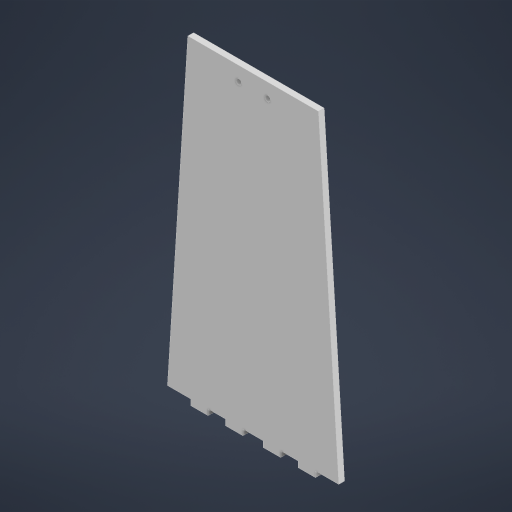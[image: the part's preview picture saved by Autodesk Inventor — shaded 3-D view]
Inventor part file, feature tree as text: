
AUTODESK INVENTOR PART (.ipt)
format: ipt  version: 2023.2 (Build 272271000, 271)  size: 237,056 bytes
history: native  units: mm
features: sketch x2
ambient origin geometry x8: Origin, YZ Plane, XZ Plane, XY Plane, X Axis, Y Axis, Z Axis, Center Point
bodies: Body1 (feature_tree)
feature tree (2):
  sketch  "Sketch1"  dims[d229=90.0mm]
  sketch  "Sketch2"  dims[d232=16.0mm d233=12.0mm d234=12.0mm d235=4.0mm d237=4.0mm d238=0.0mm d239=14.0mm d241=220.0mm d242=4.0mm d244=10.0mm d245=20.0mm d246=4.0mm d247=0.0mm d9=0.5mm d10=0.872665mm d11=0.5mm d12=0.872665mm d13=0.5mm d14=0.872665mm d27=0.5mm d28=0.872665mm d29=0.5mm d30=0.872665mm d88=0.5mm d89=0.872665mm d90=0.5mm d91=0.872665mm d116=0.5mm d117=0.872665mm d118=0.5mm d119=0.872665mm d154=0.5mm d155=0.872665mm d156=0.5mm d157=0.872665mm d181=0.5mm d182=0.872665mm d183=0.5mm d184=0.872665mm d221=0.5mm d222=0.872665mm d223=0.5mm d224=0.872665mm]
